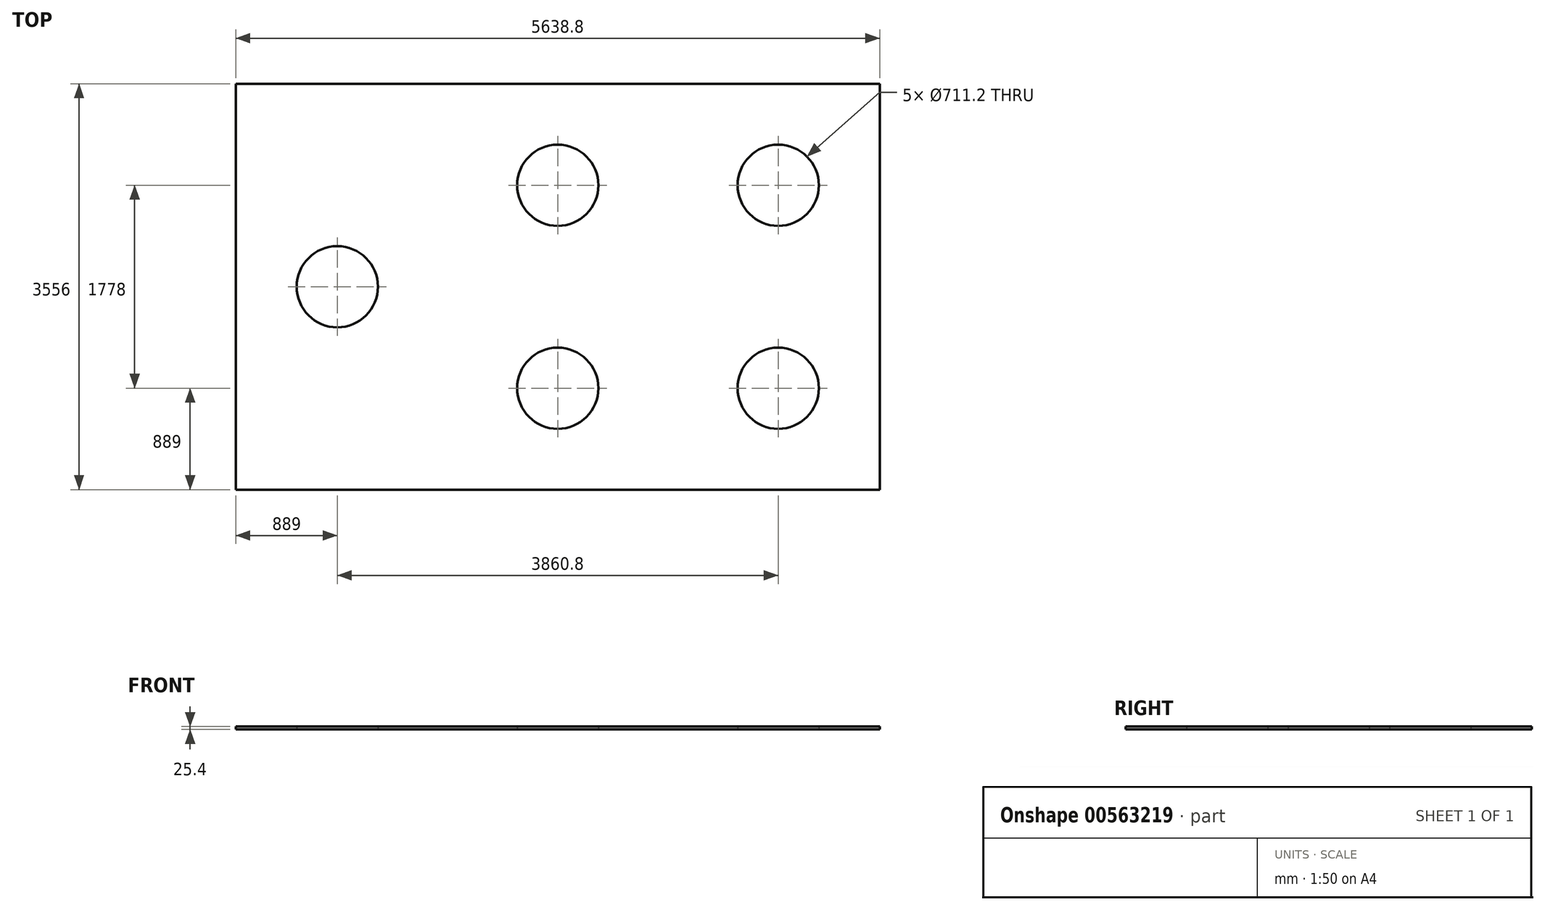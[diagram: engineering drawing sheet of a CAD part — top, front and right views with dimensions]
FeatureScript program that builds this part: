
annotation { "Feature Type Name" : "Feature", "Feature Type Description" : "" }
export const myFeature = defineFeature(function(context is Context, id is Id, definition is map)
    precondition{}
    {
        {
            var Q0;
            Q0=qCreatedBy(makeId("Top.planeOp"),FACE);
            var sketch = newSketch(context, id + "F0", { "sketchPlane" : qUnion([Q0])});
            skCircle(sketch, "E0", {"center": v(0, 0) * mm, "radius": 355.6 * mm});
            skCircle(sketch, "E1", {"center": v(0, -1778) * mm, "radius": 355.6 * mm});
            skCircle(sketch, "E2", {"center": v(-1930.4, 0) * mm, "radius": 355.6 * mm});
            skCircle(sketch, "E3", {"center": v(-1930.4, -1778) * mm, "radius": 355.6 * mm});
            skCircle(sketch, "E4", {"center": v(-3860.8, -889) * mm, "radius": 355.6 * mm});
            skLineSegment(sketch, "E5.bottom", {"start": v(889, 889) * mm, "end": v(-4749.8, 889) * mm});
            skLineSegment(sketch, "E5.top", {"start": v(889, -2667) * mm, "end": v(-4749.8, -2667) * mm});
            skLineSegment(sketch, "E5.left", {"start": v(889, 889) * mm, "end": v(889, -2667) * mm});
            skLineSegment(sketch, "E5.right", {"start": v(-4749.8, 889) * mm, "end": v(-4749.8, -2667) * mm});
            skSolve(sketch);
        }
        {
            var Q0;
            Q0=makeQuery(id+"F0.imprint","IMPRINT",FACE,{"disambiguationData":[TD([[makeQuery(id+"F0.imprint","IMPRINT",EDGE,{"derivedFrom":sQuery(id+"F0.wireOp",EDGE,"E0")}),-1.0]])]});
            extrude(context, id + "F1", {"entities" : qUnion([Q0]), "depth" : 25.4 * mm, "offsetDistance" : 25.4 * mm});
        }
    });
